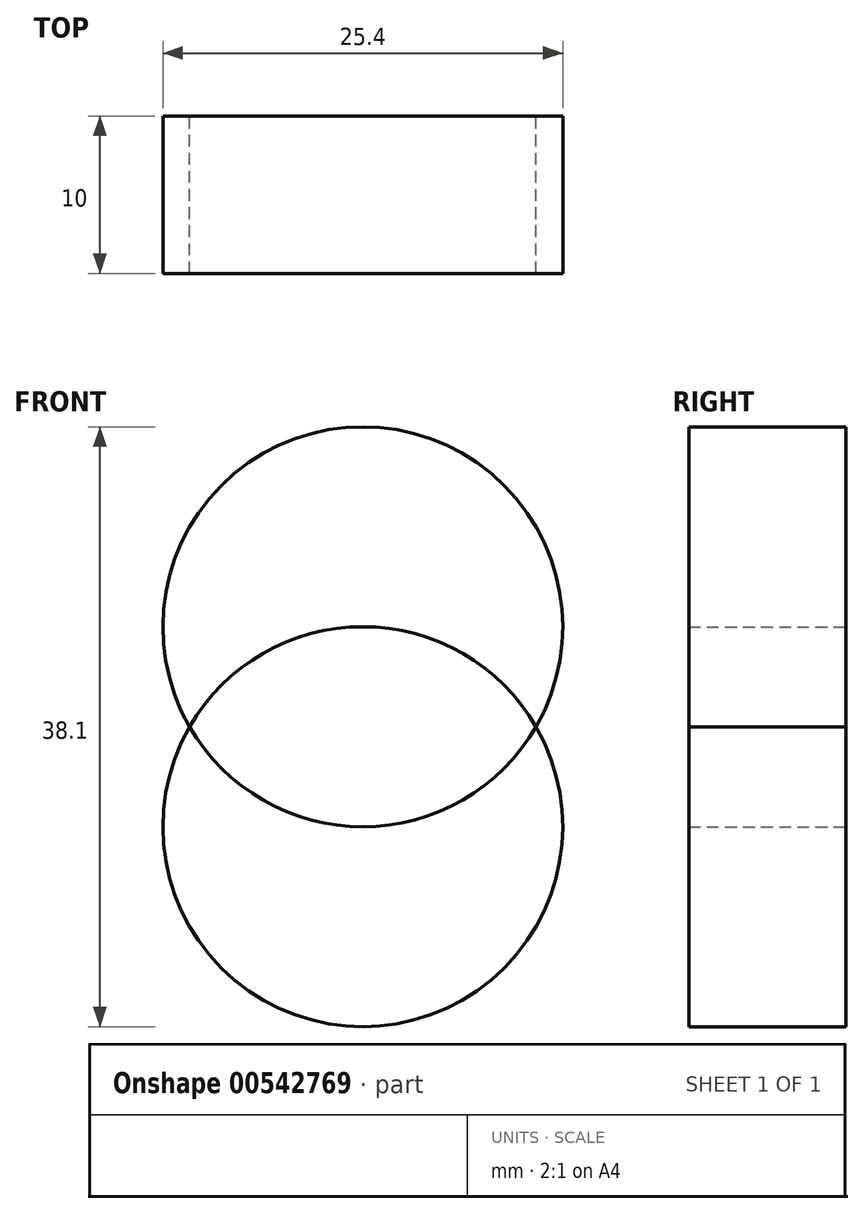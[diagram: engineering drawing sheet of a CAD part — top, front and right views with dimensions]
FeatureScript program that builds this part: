
annotation { "Feature Type Name" : "Feature", "Feature Type Description" : "" }
export const myFeature = defineFeature(function(context is Context, id is Id, definition is map)
    precondition{}
    {
        {
            var Q0;
            Q0=qCreatedBy(makeId("Front.planeOp"),FACE);
            var sketch = newSketch(context, id + "F0", { "sketchPlane" : qUnion([Q0])});
            skCircle(sketch, "E0", {"center": v(0, -6.35) * mm, "radius": 12.7 * mm});
            skCircle(sketch, "E1", {"center": v(0, 6.35) * mm, "radius": 12.7 * mm});
            skLineSegment(sketch, "E2.bottom", {"start": v(-19.05, 22.22) * mm, "end": v(19.05, 22.22) * mm});
            skLineSegment(sketch, "E2.top", {"start": v(-19.05, -22.23) * mm, "end": v(19.05, -22.23) * mm});
            skLineSegment(sketch, "E2.left", {"start": v(-19.05, 22.22) * mm, "end": v(-19.05, -22.23) * mm});
            skLineSegment(sketch, "E2.right", {"start": v(19.05, 22.22) * mm, "end": v(19.05, -22.23) * mm});
            skPoint(sketch, "E2.middle", {"position": v(0, 0) * mm});
            skSolve(sketch);
        }
        {
            var Q0;
            Q0=makeQuery(id+"F0.imprint","IMPRINT",FACE,{"disambiguationData":[TD([[makeQuery(id+"F0.imprint","IMPRINT",EDGE,{"derivedFrom":sQuery(id+"F0.wireOp",EDGE,"E0")}),-1.0]])]});
            var Q1;
            {var subQ0=sQuery(id+"F0.wireOp",EDGE,"E1");var subQ1=sQuery(id+"F0.wireOp",EDGE,"E0");var subQ2=makeQuery(id+"F0.imprint","INTERSECT",VERTEX,{"disambiguationData":[OD(0.0)],"derivedFrom":[subQ1,subQ0]});Q1=makeQuery(id+"F0.imprint","IMPRINT",FACE,{"disambiguationData":[TD([[makeQuery(id+"F0.imprint","IMPRINT",EDGE,{"disambiguationData":[TD([[subQ2,-1.0]])],"derivedFrom":subQ1}),1.0]])]});}
            extrude(context, id + "F1", {"entities" : qUnion([Q0, Q1]), "endBound" : BoundingType.SYMMETRIC, "depth" : 10 * mm, "offsetDistance" : 25 * mm});
        }
    });
